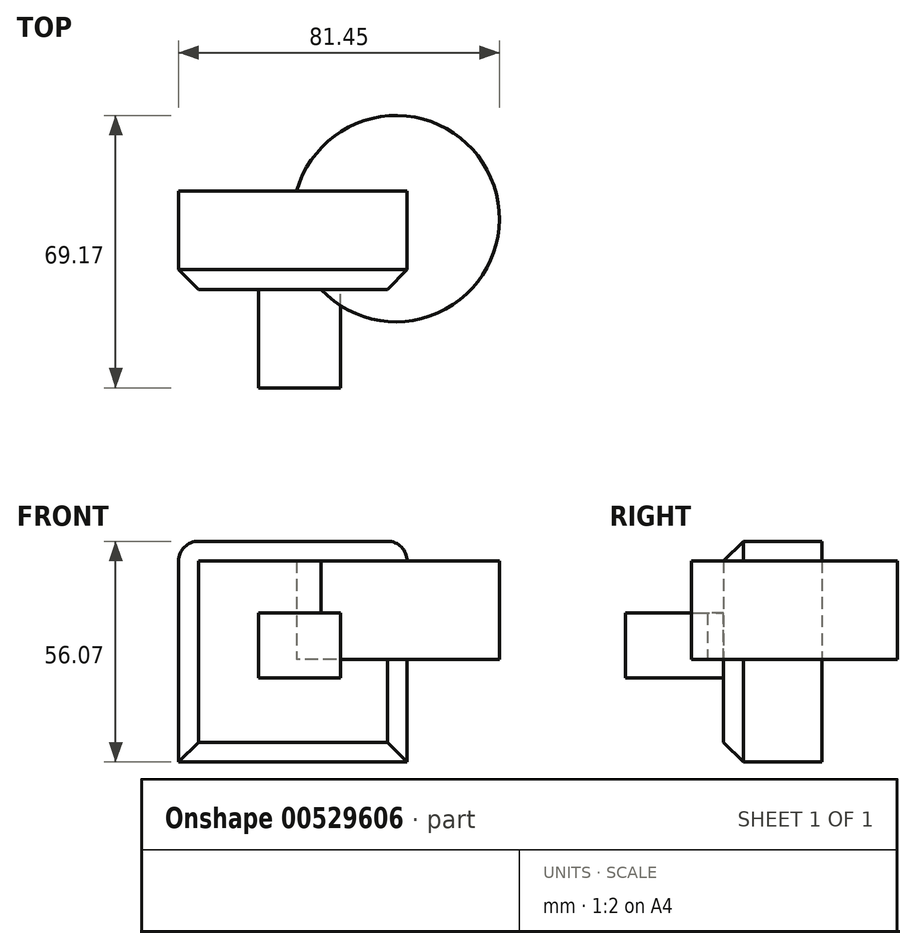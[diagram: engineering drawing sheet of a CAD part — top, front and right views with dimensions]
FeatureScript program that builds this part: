
annotation { "Feature Type Name" : "Feature", "Feature Type Description" : "" }
export const myFeature = defineFeature(function(context is Context, id is Id, definition is map)
    precondition{}
    {
        {
            var Q0;
            Q0=qCreatedBy(makeId("Front.planeOp"),FACE);
            var sketch = newSketch(context, id + "F0", { "sketchPlane" : qUnion([Q0])});
            skLineSegment(sketch, "E0.bottom", {"start": v(-25, 30) * mm, "end": v(23.04, 30) * mm});
            skLineSegment(sketch, "E0.top", {"start": v(-30, -26.07) * mm, "end": v(28.04, -26.07) * mm});
            skLineSegment(sketch, "E0.left", {"start": v(-30, 25) * mm, "end": v(-30, -26.07) * mm});
            skLineSegment(sketch, "E0.right", {"start": v(28.04, 25) * mm, "end": v(28.04, -26.07) * mm});
            skPoint(sketch, "E1.visualSharp", {"position": v(-30, 30) * mm});
            skArc(sketch, "E1.filletArc", {"start": v(-25, 30) * mm, "mid": v(-28.54, 28.54) * mm, "end": v(-30, 25) * mm});
            skPoint(sketch, "E2.visualSharp", {"position": v(28.04, 30) * mm});
            skArc(sketch, "E2.filletArc", {"start": v(28.04, 25) * mm, "mid": v(26.57, 28.54) * mm, "end": v(23.04, 30) * mm});
            skSolve(sketch);
        }
        {
            var Q0;
            Q0=makeQuery(id+"F0.imprint","IMPRINT",FACE,{"disambiguationData":[TD([[makeQuery(id+"F0.imprint","IMPRINT",EDGE,{"derivedFrom":sQuery(id+"F0.wireOp",EDGE,"E0.bottom")}),-1.0]])]});
            extrude(context, id + "F1", {"entities" : qUnion([Q0]), "depth" : 25 * mm, "offsetDistance" : 25 * mm});
        }
        {
            var Q0;
            Q0=makeQuery(id+"F1.opExtrude","CAP_EDGE",EDGE,{"disambiguationData":[OSD([sQuery(id+"F0.wireOp",EDGE,"E0.left")])],"isStart":false});
            var Q1;
            Q1=makeQuery(id+"F1.opExtrude","CAP_EDGE",EDGE,{"disambiguationData":[OSD([sQuery(id+"F0.wireOp",EDGE,"E0.top")])],"isStart":false});
            chamfer(context, id + "F2", {"entities" : qUnion([Q0, Q1]), "width" : 5 * mm, "tangentPropagation" : true});
        }
        {
            var Q0;
            Q0=makeQuery(id+"F1.opExtrude","CAP_FACE",FACE,{"disambiguationData":[OSD([sQuery(id+"F0.wireOp",EDGE,"E0.bottom"),sQuery(id+"F0.wireOp",EDGE,"E0.top"),sQuery(id+"F0.wireOp",EDGE,"E0.left"),sQuery(id+"F0.wireOp",EDGE,"E0.right"),sQuery(id+"F0.wireOp",EDGE,"E1.filletArc"),sQuery(id+"F0.wireOp",EDGE,"E2.filletArc")])],"isStart":false});
            var sketch = newSketch(context, id + "F3", { "sketchPlane" : qUnion([Q0])});
            skLineSegment(sketch, "E3.bottom", {"start": v(-9.72, -4.78) * mm, "end": v(11.13, -4.78) * mm});
            skLineSegment(sketch, "E3.top", {"start": v(-9.72, 11.75) * mm, "end": v(11.13, 11.75) * mm});
            skLineSegment(sketch, "E3.left", {"start": v(-9.72, -4.78) * mm, "end": v(-9.72, 11.75) * mm});
            skLineSegment(sketch, "E3.right", {"start": v(11.13, -4.78) * mm, "end": v(11.13, 11.75) * mm});
            skPoint(sketch, "E4.firstSnap0", {"position": v(-9.72, 3.49) * mm});
            skPoint(sketch, "E4.oppositeSnap0", {"position": v(-9.72, 3.49) * mm});
            skLineSegment(sketch, "E4.bottom", {"start": v(-13.1, 3.49) * mm, "end": v(4.36, 3.49) * mm});
            skLineSegment(sketch, "E4.top", {"start": v(-13.1, 3.49) * mm, "end": v(4.36, 3.49) * mm});
            skLineSegment(sketch, "E4.left", {"start": v(-13.1, 3.49) * mm, "end": v(-13.1, 3.49) * mm});
            skLineSegment(sketch, "E4.right", {"start": v(4.36, 3.49) * mm, "end": v(4.36, 3.49) * mm});
            skSolve(sketch);
        }
        {
            var Q0;
            {var subQ3=sQuery(id+"F3.wireOp",EDGE,"E3.bottom");Q0=makeQuery(id+"F3.imprint","IMPRINT",FACE,{"disambiguationData":[TD([[makeQuery(id+"F3.imprint","IMPRINT",EDGE,{"derivedFrom":subQ3}),1.0]])]});}
            extrude(context, id + "F4", {"entities" : qUnion([Q0]), "operationType" : NewBodyOperationType.ADD, "depth" : 25 * mm, "offsetDistance" : 25 * mm});
        }
        {
            var Q0;
            Q0=qCreatedBy(makeId("Top.planeOp"),FACE);
            var sketch = newSketch(context, id + "F5", { "sketchPlane" : qUnion([Q0])});
            skCircle(sketch, "E5", {"center": v(-7.2, -7.92) * mm, "radius": 10.7 * mm});
            skCircle(sketch, "E6", {"center": v(25.24, -7.03) * mm, "radius": 26.2 * mm});
            skSolve(sketch);
        }
        {
            var Q0;
            {var subQ0=sQuery(id+"F5.wireOp",EDGE,"E6");var subQ1=sQuery(id+"F5.wireOp",EDGE,"E5");var subQ2=makeQuery(id+"F5.imprint","INTERSECT",VERTEX,{"disambiguationData":[OD(0.0)],"derivedFrom":[subQ1,subQ0]});Q0=makeQuery(id+"F5.imprint","IMPRINT",FACE,{"disambiguationData":[TD([[makeQuery(id+"F5.imprint","IMPRINT",EDGE,{"disambiguationData":[TD([[subQ2,-1.0]])],"derivedFrom":subQ1}),-1.0]])]});}
            extrude(context, id + "F6", {"entities" : qUnion([Q0]), "operationType" : NewBodyOperationType.ADD, "depth" : 25 * mm, "offsetDistance" : 25 * mm});
        }
    });
